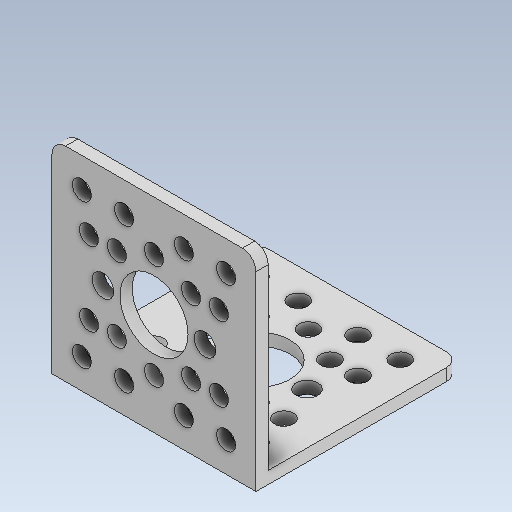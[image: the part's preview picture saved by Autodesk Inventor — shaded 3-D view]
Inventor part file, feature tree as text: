
AUTODESK INVENTOR PART (.ipt)
format: ipt  version: 2020 (Build 240168000, 168)  size: 194,560 bytes
history: native  units: in
note: dims shown in document units (in); Inventor stores cm internally (conversion verified against a paired STEP export)
features: fillet x1
ambient origin geometry x8: Origin, YZ Plane, XZ Plane, XY Plane, X Axis, Y Axis, Z Axis, Center Point
bodies: Solid1 (feature_tree)
feature tree (1):
  fillet  "Fillet1"  [1 undecoded]
note: 1 required parameter value undecoded (feature->parameter linkage not recoverable at this tier; creation-order binding heuristic only, values carry confidence <= 0.55)
